# Revit family: porta_fit_H1
name_source: partatom
category: Drzwi
revit_build: Autodesk Revit 2016 (Build: 20150714_1515(x64)
units: mm (PartAtom-declared; Revit-internal decimal feet)

## family parameters
Obiekt nadrzędny = Ściana
Punkt obliczania pomieszczeń = Nie
Tnij formami wycięć po wczytaniu = Nie
Współdzielony = Nie
Zawsze pionowo = Tak

## types (5) — shared parameters
Funkcja = Wewnętrzna
Hs = 2030 mm  [stored 6.6601 ft]
Informacja = Własność Porta KMI Poland, wszelkie prawa zastrzeżone.
Konstrukcja analityczna = <Brak>
Producent = PORTA KMI POLAND
Wysokość = 2060 mm  [stored 6.75853 ft]
Zakończenie ściany = Wg obiektu nadrzędnego

## per-type parameters (varying)
| type | Opis | Sb | Ss | Szerokość | URL |
| PN 70 |  | 746 mm | 744 mm | 780 mm | www.porta.com.pl |
| PN 60 |  | 646 mm | 644 mm  [stored 2.11286 ft] | 680 mm | www.porta.com.pl , www.portadoors.com , www.portacad.eu |
| PN 80 | Biblioteki CAD produktów firmy PORTA KMI POLAND S.A. wraz z ich wizualizacjami są chronione prawami własności przemysłowej i intelektualnej. Można je wykorzystywać do handlowych celów osobistych poprzez zastosowanie w projektach, jednak nie wolno ich powielać, modyfikować, licencjonować ani publikować, w całości ani w części, chyba że celem przeglądania, bez uprzedniej pisemnej zgody PORTA KMI Poland sp.z.o.o. www.porta.com.pl | 846 mm | 844 mm | 880 mm | www.porta.com.pl , www.portadoors.com , www.portacad.eu |
| PN 90 |  | 946 mm  [stored 3.10367 ft] | 944 mm | 980 mm  [stored 3.21522 ft] | www.porta.com.pl |
| PN 100 |  | 1046 mm | 1044 mm | 1080 mm | www.porta.com.pl , www.portadoors.com , www.portacad.eu |

note: [stored X ft] marks values corroborated as IEEE doubles in the binary element streams (Revit-internal decimal feet)

## geometry (parser evidence)
native form markers: Blend x4, Sweep x3
no freeform markers — native parametric forms only
